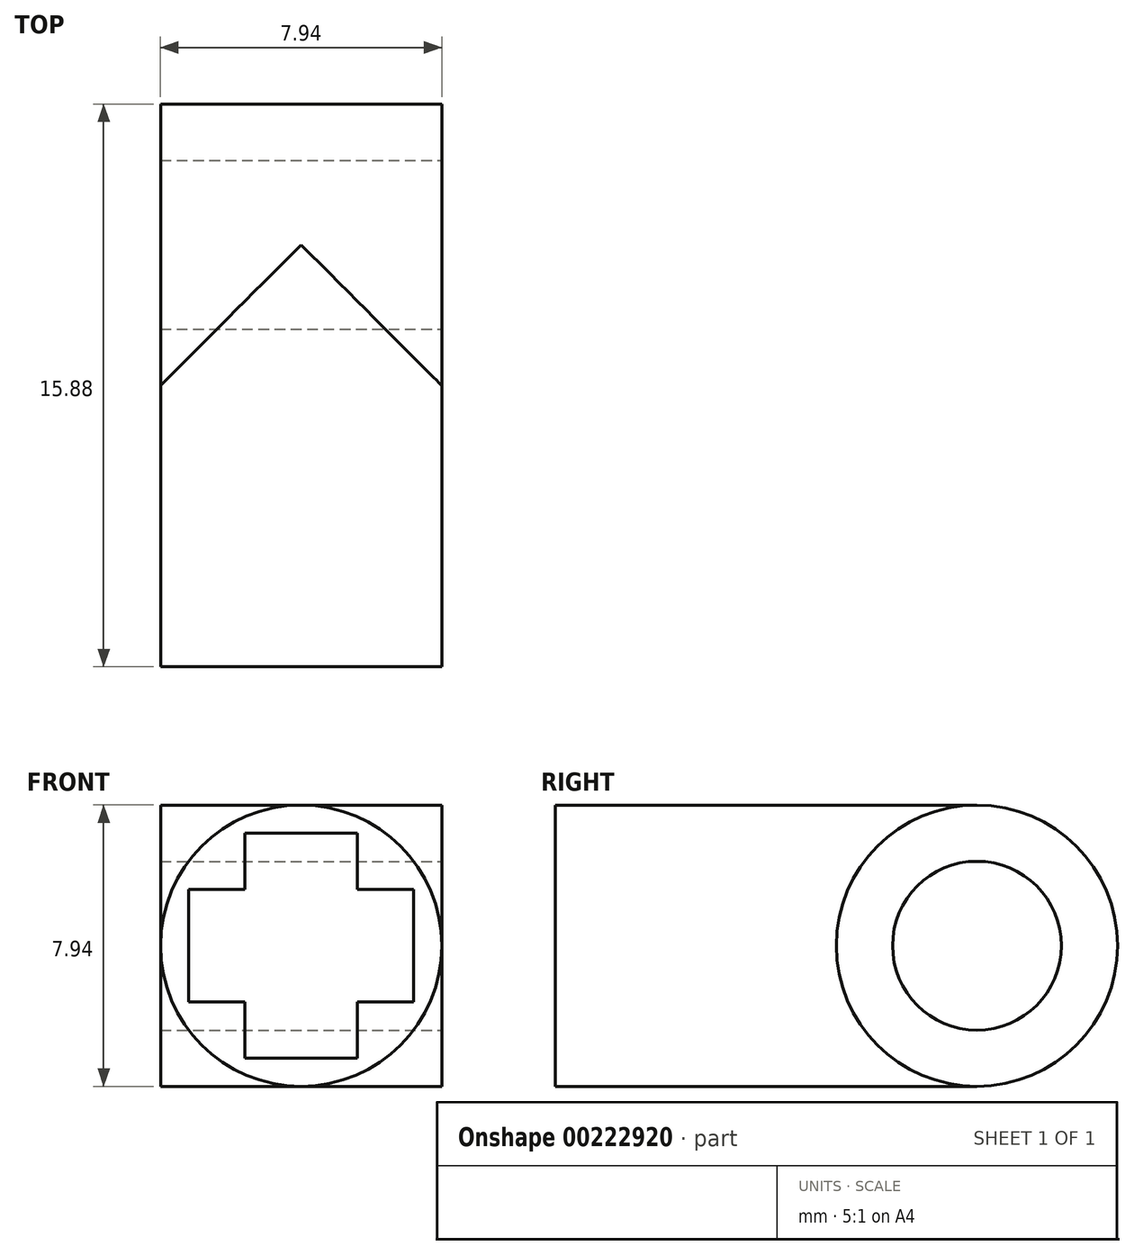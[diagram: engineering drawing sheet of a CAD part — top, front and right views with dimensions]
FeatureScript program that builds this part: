
annotation { "Feature Type Name" : "Feature", "Feature Type Description" : "" }
export const myFeature = defineFeature(function(context is Context, id is Id, definition is map)
    precondition{}
    {
        {
            var Q0;
            Q0=qCreatedBy(makeId("Top.planeOp"),FACE);
            var sketch = newSketch(context, id + "F0", { "sketchPlane" : qUnion([Q0])});
            skLineSegment(sketch, "E0.bottom", {"start": v(0, 0) * mm, "end": v(-3.97, 0) * mm});
            skLineSegment(sketch, "E0.top", {"start": v(0, 7.94) * mm, "end": v(-3.97, 7.94) * mm});
            skLineSegment(sketch, "E0.left", {"start": v(0, 0) * mm, "end": v(0, 7.94) * mm});
            skLineSegment(sketch, "E0.right", {"start": v(-3.97, 0) * mm, "end": v(-3.97, 7.94) * mm});
            skLineSegment(sketch, "E1.top", {"start": v(0, 9.53) * mm, "end": v(-3.97, 9.53) * mm});
            skLineSegment(sketch, "E1.right", {"start": v(-3.97, 7.94) * mm, "end": v(-3.97, 9.53) * mm});
            skLineSegment(sketch, "E2.top", {"start": v(0, 11.9) * mm, "end": v(-3.97, 11.9) * mm});
            skLineSegment(sketch, "E2.left", {"start": v(0, 9.52) * mm, "end": v(0, 11.9) * mm});
            skLineSegment(sketch, "E2.right", {"start": v(-3.97, 9.53) * mm, "end": v(-3.97, 11.9) * mm});
            skLineSegment(sketch, "E3.MirrorCS", {"start": v(0, 9.52) * mm, "end": v(0, 14.29) * mm});
            skLineSegment(sketch, "E4.MirrorCS", {"start": v(0, 11.9) * mm, "end": v(3.97, 11.9) * mm});
            skLineSegment(sketch, "E5.MirrorCS", {"start": v(0, 9.53) * mm, "end": v(3.97, 9.53) * mm});
            skLineSegment(sketch, "E6.MirrorCS", {"start": v(0, 7.94) * mm, "end": v(3.97, 7.94) * mm});
            skLineSegment(sketch, "E7.MirrorCS", {"start": v(3.97, 7.94) * mm, "end": v(3.97, 9.53) * mm});
            skLineSegment(sketch, "E8.MirrorCS", {"start": v(3.97, 9.53) * mm, "end": v(3.97, 14.29) * mm});
            skLineSegment(sketch, "E9", {"start": v(0, 7.94) * mm, "end": v(0, 9.53) * mm});
            skSolve(sketch);
        }
        {
            var Q0;
            Q0=makeQuery(id+"F0.imprint","IMPRINT",FACE,{"disambiguationData":[TD([[makeQuery(id+"F0.imprint","IMPRINT",EDGE,{"derivedFrom":sQuery(id+"F0.wireOp",EDGE,"E0.bottom")}),-1.0]])]});
            var Q1;
            Q1=makeQuery(id+"F0.imprint","IMPRINT",FACE,{"disambiguationData":[TD([[makeQuery(id+"F0.imprint","IMPRINT",EDGE,{"derivedFrom":sQuery(id+"F0.wireOp",EDGE,"E0.top")}),-1.0]])]});
            var Q2;
            Q2=sQuery(id+"F0.wireOp",EDGE,"E0.left");
            revolve(context, id + "F1", {"entities" : qUnion([Q0, Q1]), "axis" : qUnion([Q2]), "revolveType" : RevolveType.FULL});
        }
        {
            var Q0;
            Q0=makeQuery(id+"F0.imprint","IMPRINT",FACE,{"disambiguationData":[TD([[makeQuery(id+"F0.imprint","IMPRINT",EDGE,{"derivedFrom":sQuery(id+"F0.wireOp",EDGE,"E0.top")}),-1.0]])]});
            var Q1;
            Q1=makeQuery(id+"F0.imprint","IMPRINT",FACE,{"disambiguationData":[TD([[makeQuery(id+"F0.imprint","IMPRINT",EDGE,{"derivedFrom":sQuery(id+"F0.wireOp",EDGE,"E5.MirrorCS")}),-1.0]])]});
            var Q2;
            Q2=sQuery(id+"F0.wireOp",EDGE,"E2.top");
            revolve(context, id + "F2", {"operationType" : NewBodyOperationType.ADD, "entities" : qUnion([Q0, Q1]), "axis" : qUnion([Q2]), "revolveType" : RevolveType.FULL});
        }
        {
            var Q0;
            Q0=makeQuery(id+"F2.boolean.opBoolean","SPLIT",FACE,{"disambiguationData":[OD(1.0)],"derivedFrom":makeQuery(id+"F1.opRevolve","SWEPT_FACE",FACE,{"disambiguationData":[OSD([sQuery(id+"F0.wireOp",EDGE,"E1.top")])]})});
            var Q1;
            Q1=makeQuery(id+"F2.boolean.opBoolean","SPLIT",FACE,{"disambiguationData":[OD(0.0)],"derivedFrom":makeQuery(id+"F1.opRevolve","SWEPT_FACE",FACE,{"disambiguationData":[OSD([sQuery(id+"F0.wireOp",EDGE,"E1.top")])]})});
            extrude(context, id + "F3", {"entities" : qUnion([Q0, Q1]), "operationType" : NewBodyOperationType.ADD, "depth" : 2.38 * mm});
        }
        {
            var Q0;
            Q0=makeQuery(id+"F1.opRevolve","SWEPT_FACE",FACE,{"disambiguationData":[OSD([sQuery(id+"F0.wireOp",EDGE,"E0.bottom")])]});
            var sketch = newSketch(context, id + "F4", { "sketchPlane" : qUnion([Q0])});
            skLineSegment(sketch, "E10.bottom", {"start": v(-1.59, 3.18) * mm, "end": v(1.59, 3.18) * mm});
            skLineSegment(sketch, "E10.top", {"start": v(-1.59, -3.18) * mm, "end": v(1.59, -3.18) * mm});
            skLineSegment(sketch, "E10.left", {"start": v(-1.59, 3.18) * mm, "end": v(-1.59, -3.18) * mm});
            skLineSegment(sketch, "E10.right", {"start": v(1.59, 3.18) * mm, "end": v(1.59, -3.18) * mm});
            skPoint(sketch, "E10.middle", {"position": v(0, 0) * mm});
            skLineSegment(sketch, "E11.bottom", {"start": v(-3.17, 1.59) * mm, "end": v(3.18, 1.59) * mm});
            skLineSegment(sketch, "E11.top", {"start": v(-3.18, -1.59) * mm, "end": v(3.17, -1.59) * mm});
            skLineSegment(sketch, "E11.left", {"start": v(-3.17, 1.59) * mm, "end": v(-3.18, -1.59) * mm});
            skLineSegment(sketch, "E11.right", {"start": v(3.18, 1.59) * mm, "end": v(3.17, -1.59) * mm});
            skSolve(sketch);
        }
        {
            var Q0;
            {var subQ0=sQuery(id+"F4.wireOp",EDGE,"E11.bottom");var subQ1=sQuery(id+"F4.wireOp",EDGE,"E10.left");var subQ2=makeQuery(id+"F4.imprint","INTERSECT",VERTEX,{"derivedFrom":[subQ1,subQ0]});Q0=makeQuery(id+"F4.imprint","IMPRINT",FACE,{"disambiguationData":[TD([[makeQuery(id+"F4.imprint","IMPRINT",EDGE,{"disambiguationData":[TD([[subQ2,-1.0]])],"derivedFrom":subQ1}),1.0]])]});}
            var Q1;
            {var subQ5=sQuery(id+"F4.wireOp",EDGE,"E11.left");Q1=makeQuery(id+"F4.imprint","IMPRINT",FACE,{"disambiguationData":[TD([[makeQuery(id+"F4.imprint","IMPRINT",EDGE,{"derivedFrom":subQ5}),1.0]])]});}
            var Q2;
            {var subQ0=sQuery(id+"F4.wireOp",EDGE,"E10.bottom");Q2=makeQuery(id+"F4.imprint","IMPRINT",FACE,{"disambiguationData":[TD([[makeQuery(id+"F4.imprint","IMPRINT",EDGE,{"derivedFrom":subQ0}),-1.0]])]});}
            var Q3;
            {var subQ5=sQuery(id+"F4.wireOp",EDGE,"E11.right");Q3=makeQuery(id+"F4.imprint","IMPRINT",FACE,{"disambiguationData":[TD([[makeQuery(id+"F4.imprint","IMPRINT",EDGE,{"derivedFrom":subQ5}),-1.0]])]});}
            var Q4;
            {var subQ0=sQuery(id+"F4.wireOp",EDGE,"E10.top");Q4=makeQuery(id+"F4.imprint","IMPRINT",FACE,{"disambiguationData":[TD([[makeQuery(id+"F4.imprint","IMPRINT",EDGE,{"derivedFrom":subQ0}),1.0]])]});}
            extrude(context, id + "F5", {"entities" : qUnion([Q0, Q1, Q2, Q3, Q4]), "operationType" : NewBodyOperationType.REMOVE, "oppositeDirection" : true, "depth" : 5 / 406.4 * mm});
        }
    });
